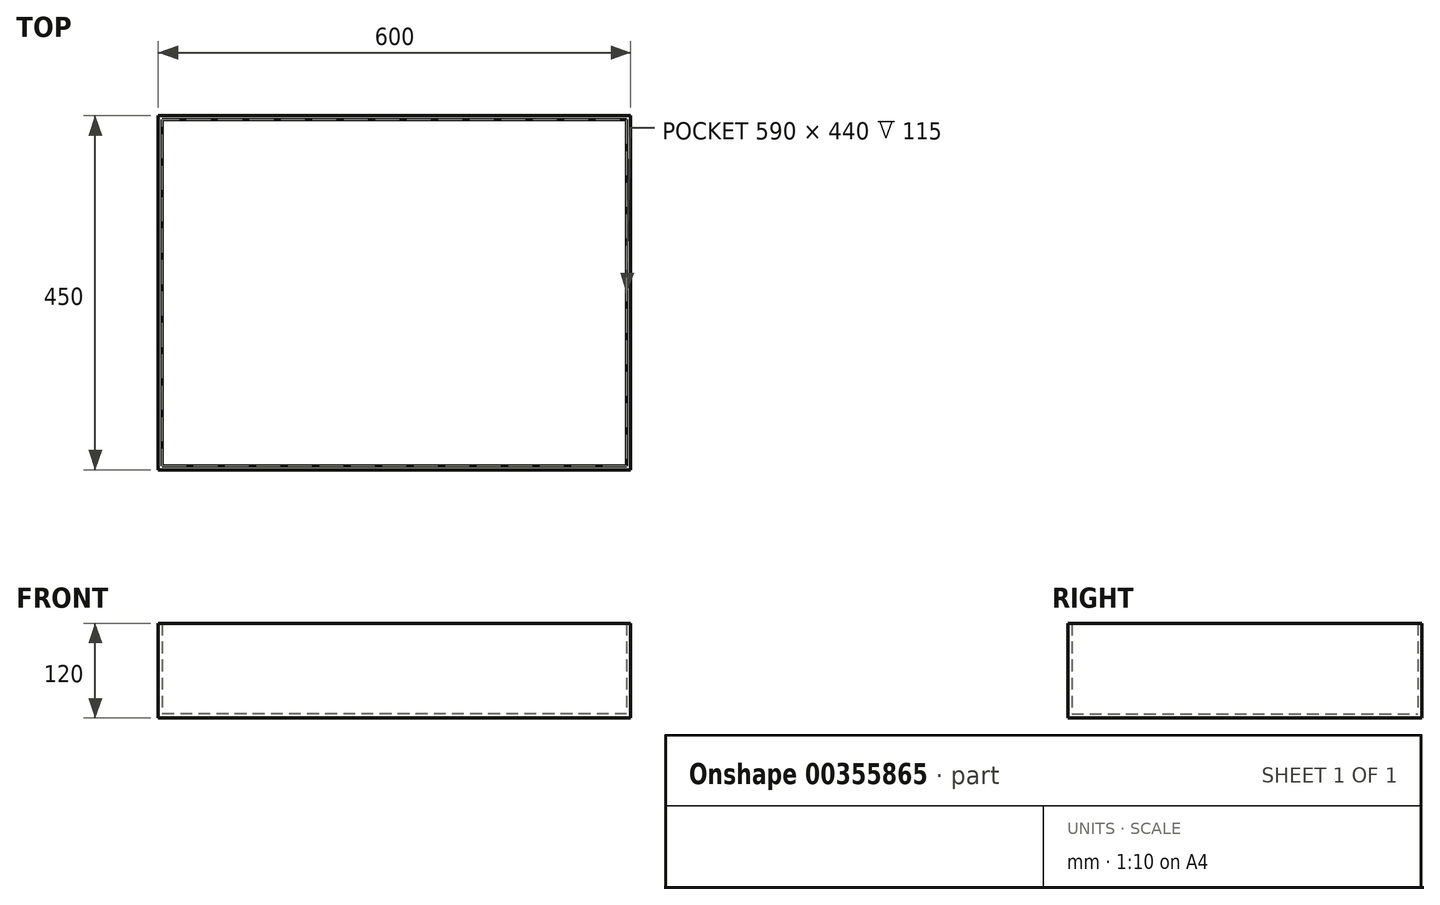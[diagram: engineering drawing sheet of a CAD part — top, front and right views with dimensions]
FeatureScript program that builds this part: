
annotation { "Feature Type Name" : "Feature", "Feature Type Description" : "" }
export const myFeature = defineFeature(function(context is Context, id is Id, definition is map)
    precondition{}
    {
        {
            var Q0;
            Q0=qCreatedBy(makeId("Top.planeOp"),FACE);
            var sketch = newSketch(context, id + "F0", { "sketchPlane" : qUnion([Q0])});
            skLineSegment(sketch, "E0.bottom", {"start": v(-37.37, 432.63) * mm, "end": v(562.63, 432.63) * mm});
            skLineSegment(sketch, "E0.top", {"start": v(-37.37, -17.37) * mm, "end": v(562.63, -17.37) * mm});
            skLineSegment(sketch, "E0.left", {"start": v(-37.37, 432.63) * mm, "end": v(-37.37, -17.37) * mm});
            skLineSegment(sketch, "E0.right", {"start": v(562.63, 432.63) * mm, "end": v(562.63, -17.37) * mm});
            skLineSegment(sketch, "E1.0", {"start": v(-32.37, 427.63) * mm, "end": v(557.63, 427.63) * mm});
            skLineSegment(sketch, "E1.1", {"start": v(-32.37, 427.63) * mm, "end": v(-32.37, -12.37) * mm});
            skLineSegment(sketch, "E1.2", {"start": v(-32.37, -12.37) * mm, "end": v(557.63, -12.37) * mm});
            skLineSegment(sketch, "E1.3", {"start": v(557.63, 427.63) * mm, "end": v(557.63, -12.37) * mm});
            skSolve(sketch);
        }
        {
            var Q0;
            Q0=makeQuery(id+"F0.imprint","IMPRINT",FACE,{"disambiguationData":[TD([[makeQuery(id+"F0.imprint","IMPRINT",EDGE,{"derivedFrom":sQuery(id+"F0.wireOp",EDGE,"E0.bottom")}),-1.0]])]});
            extrude(context, id + "F1", {"entities" : qUnion([Q0]), "depth" : 120 * mm});
        }
        {
            var Q0;
            Q0=makeQuery(id+"F1.opExtrude","CAP_FACE",FACE,{"disambiguationData":[OSD([sQuery(id+"F0.wireOp",EDGE,"E0.bottom"),sQuery(id+"F0.wireOp",EDGE,"E0.top"),sQuery(id+"F0.wireOp",EDGE,"E0.left"),sQuery(id+"F0.wireOp",EDGE,"E0.right"),sQuery(id+"F0.wireOp",EDGE,"E1.0"),sQuery(id+"F0.wireOp",EDGE,"E1.1"),sQuery(id+"F0.wireOp",EDGE,"E1.2"),sQuery(id+"F0.wireOp",EDGE,"E1.3")])],"isStart":true});
            var sketch = newSketch(context, id + "F2", { "sketchPlane" : qUnion([Q0])});
            skLineSegment(sketch, "E2.bottom", {"start": v(-37.37, 17.37) * mm, "end": v(562.63, 17.37) * mm});
            skLineSegment(sketch, "E2.top", {"start": v(-37.37, -432.63) * mm, "end": v(562.63, -432.63) * mm});
            skLineSegment(sketch, "E2.left", {"start": v(-37.37, 17.37) * mm, "end": v(-37.37, -432.63) * mm});
            skLineSegment(sketch, "E2.right", {"start": v(562.63, 17.37) * mm, "end": v(562.63, -432.63) * mm});
            skSolve(sketch);
        }
        {
            var Q0;
            Q0=qSketchRegion(id+"F2",true);
            extrude(context, id + "F3", {"entities" : qUnion([Q0]), "operationType" : NewBodyOperationType.ADD, "oppositeDirection" : true, "depth" : 5 * mm});
        }
    });
